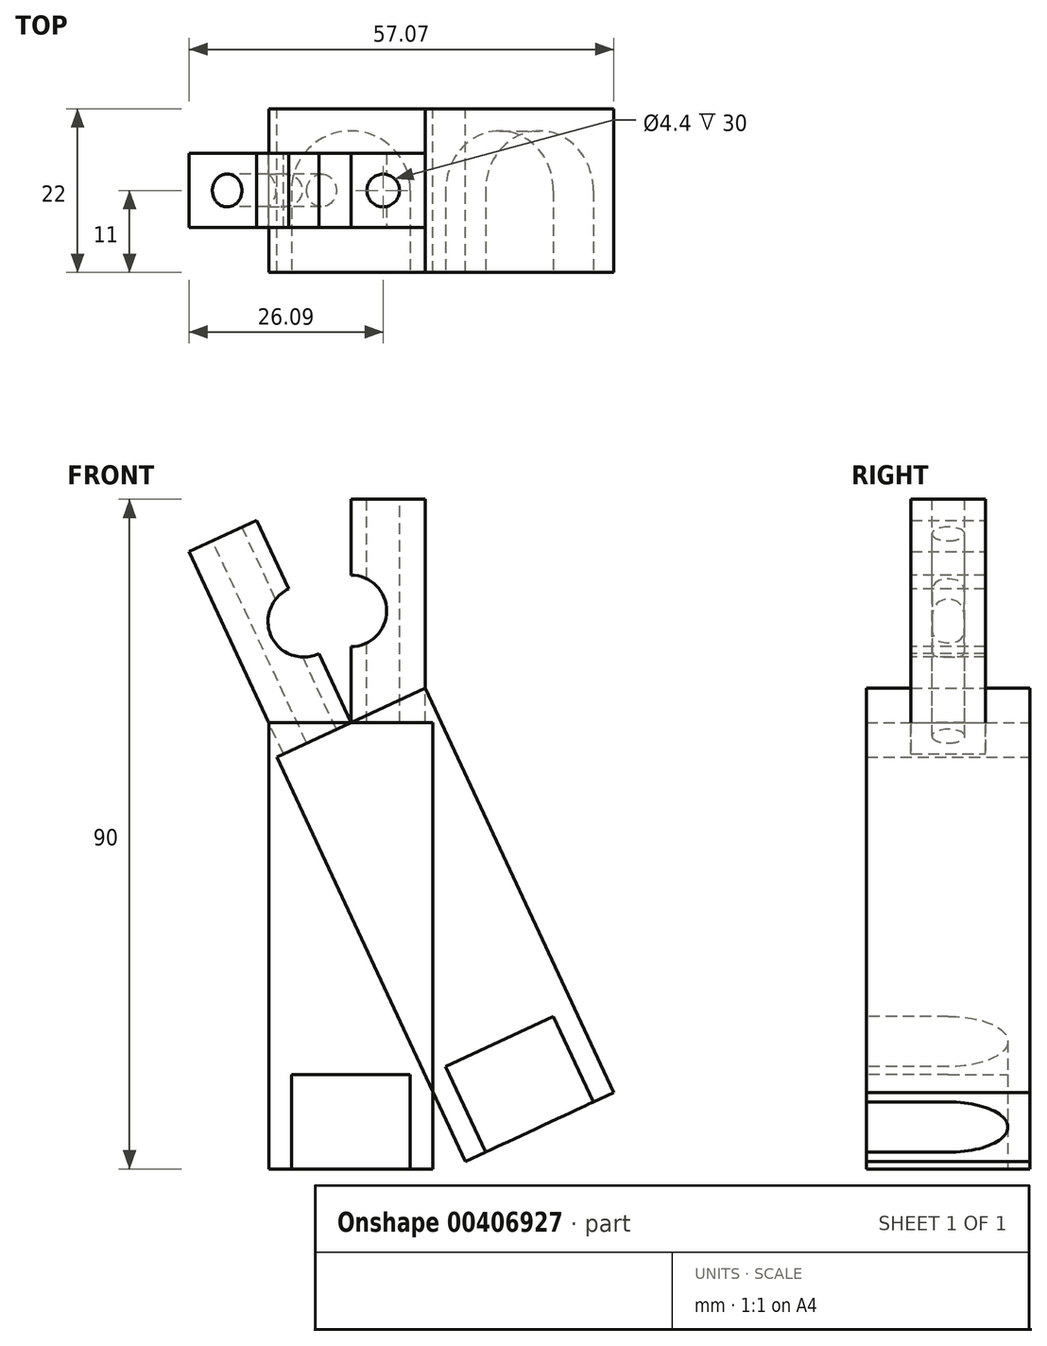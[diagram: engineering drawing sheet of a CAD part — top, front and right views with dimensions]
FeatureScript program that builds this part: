
annotation { "Feature Type Name" : "Feature", "Feature Type Description" : "" }
export const myFeature = defineFeature(function(context is Context, id is Id, definition is map)
    precondition{}
    {
        {
            var Q0;
            Q0=qCreatedBy(makeId("Front.planeOp"),FACE);
            var sketch = newSketch(context, id + "F0", { "sketchPlane" : qUnion([Q0])});
            skLineSegment(sketch, "E0.bottom", {"start": v(0, 0) * mm, "end": v(10, 0) * mm});
            skLineSegment(sketch, "E0.top", {"start": v(0, 30) * mm, "end": v(10, 30) * mm});
            skLineSegment(sketch, "E0.left", {"start": v(0, 0) * mm, "end": v(0, 30) * mm});
            skLineSegment(sketch, "E0.right", {"start": v(10, 0) * mm, "end": v(10, 30) * mm});
            skCircle(sketch, "E1", {"center": v(0, 15) * mm, "radius": 4.75 * mm, "construction": true});
            skSolve(sketch);
        }
        {
            var Q0;
            Q0 = qSketchRegion(id + "F0", true);
            extrude(context, id + "F1", {"entities" : qUnion([Q0]), "endBound" : BoundingType.SYMMETRIC, "depth" : 10 * mm});
        }
        {
            var Q0;
            Q0=makeQuery(id+"F1.opExtrude","CAP_FACE",FACE,{"disambiguationData":[OSD([sQuery(id+"F0.wireOp",EDGE,"E0.bottom"),sQuery(id+"F0.wireOp",EDGE,"E0.top"),sQuery(id+"F0.wireOp",EDGE,"E0.left"),sQuery(id+"F0.wireOp",EDGE,"E0.right")])],"isStart":false});
            var sketch = newSketch(context, id + "F2", { "sketchPlane" : qUnion([Q0])});
            skCircle(sketch, "E2", {"center": v(0, 15) * mm, "radius": 4.8 * mm});
            skSolve(sketch);
        }
        {
            var Q0;
            Q0 = qSketchRegion(id + "F2", true);
            extrude(context, id + "F3", {"entities" : qUnion([Q0]), "operationType" : NewBodyOperationType.REMOVE, "oppositeDirection" : true, "depth" : 25 * mm});
        }
        {
            var Q0;
            Q0=makeQuery(id+"F1.opExtrude","SWEPT_FACE",FACE,{"disambiguationData":[OSD([sQuery(id+"F0.wireOp",EDGE,"E0.top")])]});
            var sketch = newSketch(context, id + "F4", { "sketchPlane" : qUnion([Q0])});
            skCircle(sketch, "E3", {"center": v(4.35, 0) * mm, "radius": 2.2 * mm});
            skLineSegment(sketch, "E4", {"start": v(4.35, 0) * mm, "end": v(0, 0) * mm, "construction": true});
            skSolve(sketch);
        }
        {
            var Q0;
            Q0 = qSketchRegion(id + "F4", true);
            extrude(context, id + "F5", {"entities" : qUnion([Q0]), "operationType" : NewBodyOperationType.REMOVE, "oppositeDirection" : true, "depth" : 60 * mm});
        }
        {
            var Q0;
            Q0=qCreatedBy(makeId("Front.planeOp"),FACE);
            var sketch = newSketch(context, id + "F6", { "sketchPlane" : qUnion([Q0])});
            skLineSegment(sketch, "E5.bottom", {"start": v(11, 0) * mm, "end": v(-11, 0) * mm});
            skLineSegment(sketch, "E5.top", {"start": v(11, -60) * mm, "end": v(-11, -60) * mm});
            skLineSegment(sketch, "E5.left", {"start": v(11, 0) * mm, "end": v(11, -60) * mm});
            skLineSegment(sketch, "E5.right", {"start": v(-11, 0) * mm, "end": v(-11, -60) * mm});
            skPoint(sketch, "E5.middle", {"position": v(0, -30) * mm});
            skSolve(sketch);
        }
        {
            var Q0;
            Q0 = qSketchRegion(id + "F6", true);
            extrude(context, id + "F7", {"entities" : qUnion([Q0]), "operationType" : NewBodyOperationType.ADD, "endBound" : BoundingType.SYMMETRIC, "depth" : 22 * mm});
        }
        {
            var Q0;
            Q0=makeQuery(id+"F7.opExtrude","SWEPT_FACE",FACE,{"disambiguationData":[OSD([sQuery(id+"F6.wireOp",EDGE,"E5.top")])]});
            var sketch = newSketch(context, id + "F8", { "sketchPlane" : qUnion([Q0])});
            skCircle(sketch, "E6", {"center": v(0, 0) * mm, "radius": 8 * mm});
            skLineSegment(sketch, "E7", {"start": v(0, 0) * mm, "end": v(-8, 0) * mm, "construction": true});
            skPoint(sketch, "E7.endSnap0", {"position": v(-11, 0) * mm});
            skLineSegment(sketch, "E8.bottom", {"start": v(-8, 0) * mm, "end": v(8, 0) * mm});
            skLineSegment(sketch, "E8.top", {"start": v(-8, 11) * mm, "end": v(8, 11) * mm});
            skLineSegment(sketch, "E8.left", {"start": v(-8, 0) * mm, "end": v(-8, 11) * mm});
            skLineSegment(sketch, "E8.right", {"start": v(8, 0) * mm, "end": v(8, 11) * mm});
            skSolve(sketch);
        }
        {
            var Q0;
            Q0 = qSketchRegion(id + "F8", true);
            extrude(context, id + "F9", {"entities" : qUnion([Q0]), "operationType" : NewBodyOperationType.REMOVE, "oppositeDirection" : true, "depth" : (3 + 6 + 3.7) * mm});
        }
        {
            var Q0;
            Q0=qCreatedBy(makeId("Top.planeOp"),FACE);
            var sketch = newSketch(context, id + "F10", { "sketchPlane" : qUnion([Q0])});
            skLineSegment(sketch, "E9", {"start": v(0, 0) * mm, "end": v(0, -136.2) * mm, "construction": true});
            skSolve(sketch);
        }
        {
            var Q0;
            Q0=makeQuery(id+"F1.opExtrude","SWEPT_BODY",BODY,{"disambiguationData":[OSD([sQuery(id+"F0.wireOp",EDGE,"E0.bottom"),sQuery(id+"F0.wireOp",EDGE,"E0.top"),sQuery(id+"F0.wireOp",EDGE,"E0.left"),sQuery(id+"F0.wireOp",EDGE,"E0.right")])]});
            var Q1;
            Q1=qCreatedBy(makeId("Right.planeOp"),FACE);
            mirror(context, id + "F11", {"entities" : qUnion([Q0]), "mirrorPlane" : qUnion([Q1])});
        }
        {
            var Q0;
            Q0=makeQuery(id+"F11.opPattern","COPY",BODY,{"derivedFrom":makeQuery(id+"F1.opExtrude","SWEPT_BODY",BODY,{"disambiguationData":[OSD([sQuery(id+"F0.wireOp",EDGE,"E0.bottom"),sQuery(id+"F0.wireOp",EDGE,"E0.top"),sQuery(id+"F0.wireOp",EDGE,"E0.left"),sQuery(id+"F0.wireOp",EDGE,"E0.right")])]}),"instanceName":"1"});
            var Q1;
            Q1=sQuery(id+"F10.wireOp",EDGE,"E9");
            transform(context, id + "F12", {"entities" : qUnion([Q0]), "transformType" : TransformType.ROTATION, "transformAxis" : qUnion([Q1]), "angle" : 25 * degree, "makeCopy" : false});
        }
    });
